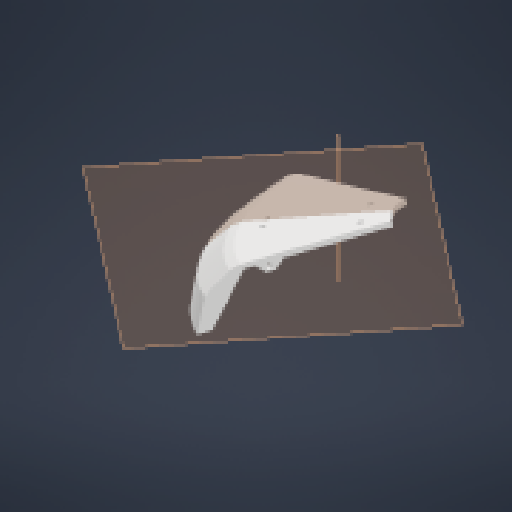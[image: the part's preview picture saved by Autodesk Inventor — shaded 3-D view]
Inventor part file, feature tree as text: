
AUTODESK INVENTOR PART (.ipt)
format: ipt  version: 2024 (Build 280153000, 153)  size: 162,816 bytes
history: native  units: in
note: dims shown in document units (in); Inventor stores cm internally (conversion verified against a paired STEP export)
features: reference x7, sketch x3, other x3, plane x2, extrude x2, revolve x1, mirror x1
ambient origin geometry x8: Origin, YZ Plane, XZ Plane, XY Plane, X Axis, Y Axis, Z Axis, Center Point
bodies: Solid1 (feature_tree)
feature tree (19):
  revolve  "Revolution1"  [1 undecoded]
  plane  "Work Plane1"
  extrude  "Extrusion1"  Depth=0.1654in
  extrude  "Extrusion2"  Depth=0.2756in TaperAngle=0.0deg
  plane  "Work Plane2"
  mirror  "Mirror1"
  sketch  "Sketch1"  dims[d0=60.0deg d1=0.2756in d2=0.0in]
  reference  "Reference1"
  reference  "Reference2"
  reference  "Reference3"
  sketch  "Sketch2"  dims[d3=0.1654in d4=0.1654in]
  reference  "Reference4"
  reference  "Reference5"
  sketch  "Sketch3"  dims[d5=0.1969in d6=0.2756in d7=0.0in]
  reference  "Reference6"
  reference  "Reference7"
  other  "<userpath>\Desktop\SeniorDesign\Head_Assembly.iam"
  other  "Head_Assembly.iam"
  other  "Head_CameraPanel_Bottom:1"
note: 1 required parameter value undecoded (feature->parameter linkage not recoverable at this tier; creation-order binding heuristic only, values carry confidence <= 0.55)
